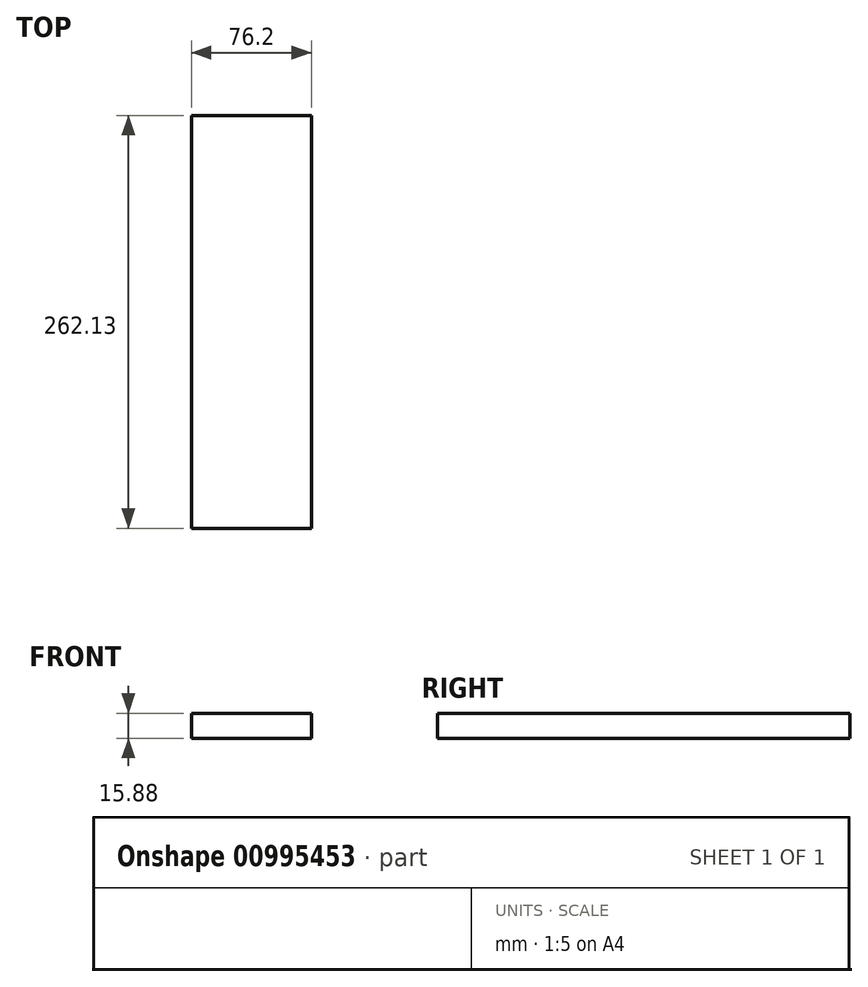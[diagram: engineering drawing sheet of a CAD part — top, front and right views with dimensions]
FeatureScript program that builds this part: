
annotation { "Feature Type Name" : "Feature", "Feature Type Description" : "" }
export const myFeature = defineFeature(function(context is Context, id is Id, definition is map)
    precondition{}
    {
        {
            var Q0;
            Q0=qCreatedBy(makeId("Front.planeOp"),FACE);
            var sketch = newSketch(context, id + "F0", { "sketchPlane" : qUnion([Q0])});
            skLineSegment(sketch, "E0.bottom", {"start": v(0, 0) * mm, "end": v(76.2, 0) * mm});
            skLineSegment(sketch, "E0.top", {"start": v(0, 15.88) * mm, "end": v(76.2, 15.88) * mm});
            skLineSegment(sketch, "E0.left", {"start": v(0, 0) * mm, "end": v(0, 15.87) * mm});
            skLineSegment(sketch, "E0.right", {"start": v(76.2, 0) * mm, "end": v(76.2, 15.87) * mm});
            skSolve(sketch);
        }
        {
            var Q0;
            Q0=makeQuery(id+"F0.imprint","IMPRINT",FACE,{"disambiguationData":[TD([[makeQuery(id+"F0.imprint","IMPRINT",EDGE,{"derivedFrom":sQuery(id+"F0.wireOp",EDGE,"E0.bottom")}),1.0]])]});
            extrude(context, id + "F1", {"entities" : qUnion([Q0]), "oppositeDirection" : true, "depth" : 262.13 * mm, "offsetDistance" : 25.4 * mm});
        }
    });
